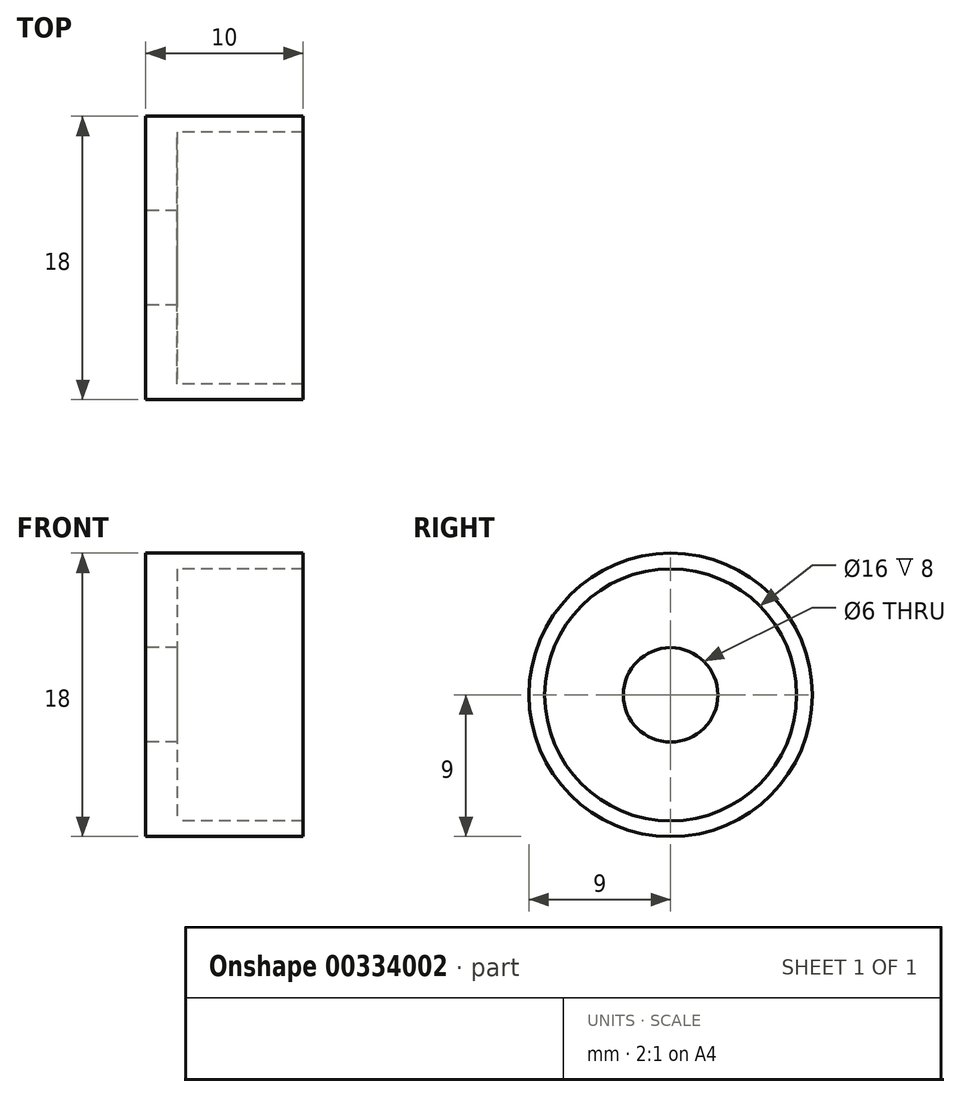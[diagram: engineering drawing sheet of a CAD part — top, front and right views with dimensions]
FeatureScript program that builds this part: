
annotation { "Feature Type Name" : "Feature", "Feature Type Description" : "" }
export const myFeature = defineFeature(function(context is Context, id is Id, definition is map)
    precondition{}
    {
        {
            var Q0;
            Q0=qCreatedBy(makeId("Top.planeOp"),FACE);
            var sketch = newSketch(context, id + "F0", { "sketchPlane" : qUnion([Q0])});
            skLineSegment(sketch, "E0", {"start": v(0, 0) * mm, "end": v(0, -8) * mm});
            skLineSegment(sketch, "E1", {"start": v(0, -8) * mm, "end": v(8, -8) * mm});
            skLineSegment(sketch, "E2", {"start": v(8, -8) * mm, "end": v(8, -9) * mm});
            skLineSegment(sketch, "E3", {"start": v(8, -9) * mm, "end": v(-2, -9) * mm});
            skLineSegment(sketch, "E4", {"start": v(-2, -9) * mm, "end": v(-2, 0) * mm});
            skLineSegment(sketch, "E5", {"start": v(-2, 0) * mm, "end": v(0, 0) * mm});
            skSolve(sketch);
        }
        {
            var Q0;
            Q0 = qSketchRegion(id + "F0", true);
            var Q1;
            Q1=sQuery(id+"F0.wireOp",EDGE,"E5");
            revolve(context, id + "F1", {"entities" : qUnion([Q0]), "axis" : qUnion([Q1]), "revolveType" : RevolveType.FULL});
        }
        {
            var Q0;
            Q0=makeQuery(id+"F1.opRevolve","SWEPT_FACE",FACE,{"disambiguationData":[OSD([sQuery(id+"F0.wireOp",EDGE,"E4")])]});
            var sketch = newSketch(context, id + "F2", { "sketchPlane" : qUnion([Q0])});
            skCircle(sketch, "E6", {"center": v(0, 0) * mm, "radius": 3 * mm});
            skSolve(sketch);
        }
        {
            var Q0;
            Q0 = qSketchRegion(id + "F2", true);
            extrude(context, id + "F3", {"entities" : qUnion([Q0]), "operationType" : NewBodyOperationType.REMOVE, "endBound" : BoundingType.UP_TO_NEXT, "oppositeDirection" : true, "depth" : 25 * mm});
        }
    });
